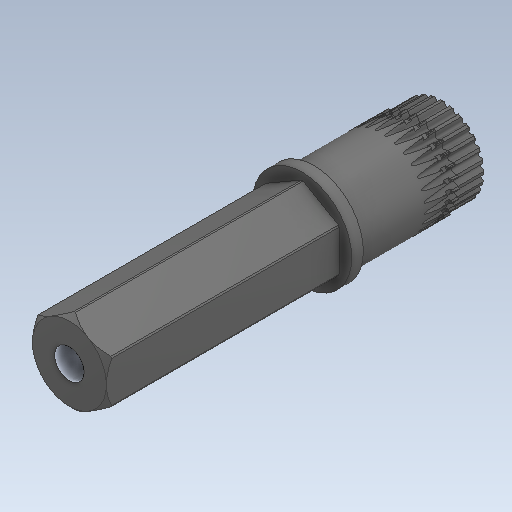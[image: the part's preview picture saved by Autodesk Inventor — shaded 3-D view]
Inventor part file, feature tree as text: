
AUTODESK INVENTOR PART (.ipt)
format: ipt  version: 2020 (Build 240168000, 168)  size: 1,429,504 bytes
history: native  units: in
note: dims shown in document units (in); Inventor stores cm internally (conversion verified against a paired STEP export)
features: fillet x1
ambient origin geometry x8: Origin, YZ Plane, XZ Plane, XY Plane, X Axis, Y Axis, Z Axis, Center Point
bodies: Solid1 (feature_tree)
feature tree (1):
  fillet  "Fillet5"  [1 undecoded]
note: 1 required parameter value undecoded (feature->parameter linkage not recoverable at this tier; creation-order binding heuristic only, values carry confidence <= 0.55)
